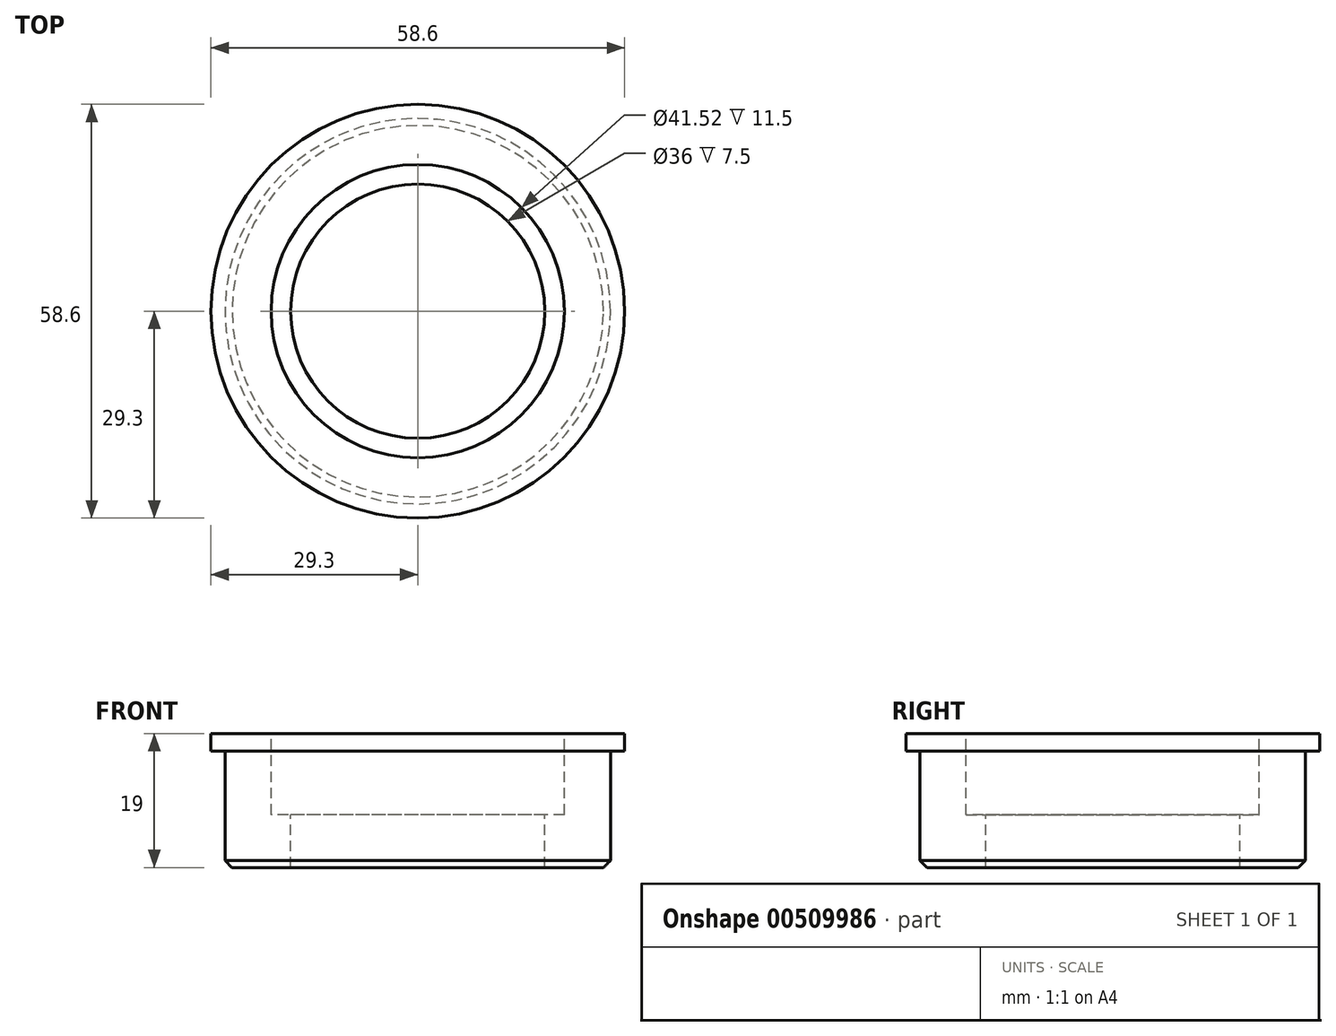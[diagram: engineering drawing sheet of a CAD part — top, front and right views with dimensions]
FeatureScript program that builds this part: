
annotation { "Feature Type Name" : "Feature", "Feature Type Description" : "" }
export const myFeature = defineFeature(function(context is Context, id is Id, definition is map)
    precondition{}
    {
        {
            var Q0;
            Q0=qCreatedBy(makeId("Top.planeOp"),FACE);
            var sketch = newSketch(context, id + "F0", { "sketchPlane" : qUnion([Q0])});
            skCircle(sketch, "E0", {"center": v(0, 0) * mm, "radius": 27.3 * mm});
            skSolve(sketch);
        }
        {
            var Q0;
            Q0 = qSketchRegion(id + "F0", true);
            extrude(context, id + "F1", {"entities" : qUnion([Q0]), "depth" : 19 * mm});
        }
        {
            var Q0;
            Q0=makeQuery(id+"F1.opExtrude","CAP_FACE",FACE,{"disambiguationData":[OSD([sQuery(id+"F0.wireOp",EDGE,"E0")])],"isStart":false});
            var sketch = newSketch(context, id + "F2", { "sketchPlane" : qUnion([Q0])});
            skCircle(sketch, "E1", {"center": v(0, 0) * mm, "radius": 20.76 * mm});
            skSolve(sketch);
        }
        {
            var Q0;
            Q0 = qSketchRegion(id + "F2", true);
            extrude(context, id + "F3", {"entities" : qUnion([Q0]), "operationType" : NewBodyOperationType.REMOVE, "oppositeDirection" : true, "depth" : 11.5 * mm, "offsetDistance" : 25 * mm});
        }
        {
            var Q0;
            Q0=makeQuery(id+"F3.boolean.opBoolean","COPY",FACE,{"derivedFrom":makeQuery(id+"F3.opExtrude","CAP_FACE",FACE,{"disambiguationData":[OSD([sQuery(id+"F2.wireOp",EDGE,"E1")])],"isStart":false})});
            var sketch = newSketch(context, id + "F4", { "sketchPlane" : qUnion([Q0])});
            skCircle(sketch, "E2", {"center": v(0, 0) * mm, "radius": 18 * mm});
            skSolve(sketch);
        }
        {
            var Q0;
            Q0 = qSketchRegion(id + "F4", true);
            extrude(context, id + "F5", {"entities" : qUnion([Q0]), "operationType" : NewBodyOperationType.REMOVE, "endBound" : BoundingType.THROUGH_ALL, "oppositeDirection" : true, "depth" : 25 * mm});
        }
        {
            var Q0;
            Q0=makeQuery(id+"F1.opExtrude","CAP_FACE",FACE,{"disambiguationData":[OSD([sQuery(id+"F0.wireOp",EDGE,"E0")])],"isStart":false});
            var sketch = newSketch(context, id + "F6", { "sketchPlane" : qUnion([Q0])});
            skCircle(sketch, "E3.0", {"center": v(0, 0) * mm, "radius": 29.3 * mm});
            skCircle(sketch, "E4.0", {"center": v(0, 0) * mm, "radius": 27.3 * mm});
            skSolve(sketch);
        }
        {
            var Q0;
            Q0 = qSketchRegion(id + "F6", true);
            extrude(context, id + "F7", {"entities" : qUnion([Q0]), "operationType" : NewBodyOperationType.ADD, "oppositeDirection" : true, "depth" : 2.5 * mm});
        }
        {
            var Q0;
            Q0=makeQuery(id+"F1.opExtrude","CAP_EDGE",EDGE,{"disambiguationData":[OSD([sQuery(id+"F0.wireOp",EDGE,"E0")])],"isStart":true});
            var Q1;
            Q1=makeQuery(id+"F3.boolean.opBoolean","COPY",EDGE,{"derivedFrom":makeQuery(id+"F3.opExtrude","CAP_EDGE",EDGE,{"disambiguationData":[OSD([sQuery(id+"F2.wireOp",EDGE,"E1")])],"isStart":true})});
            chamfer(context, id + "F8", {"entities" : qUnion([Q0, Q1]), "width" : 1 * mm, "tangentPropagation" : true});
        }
    });
